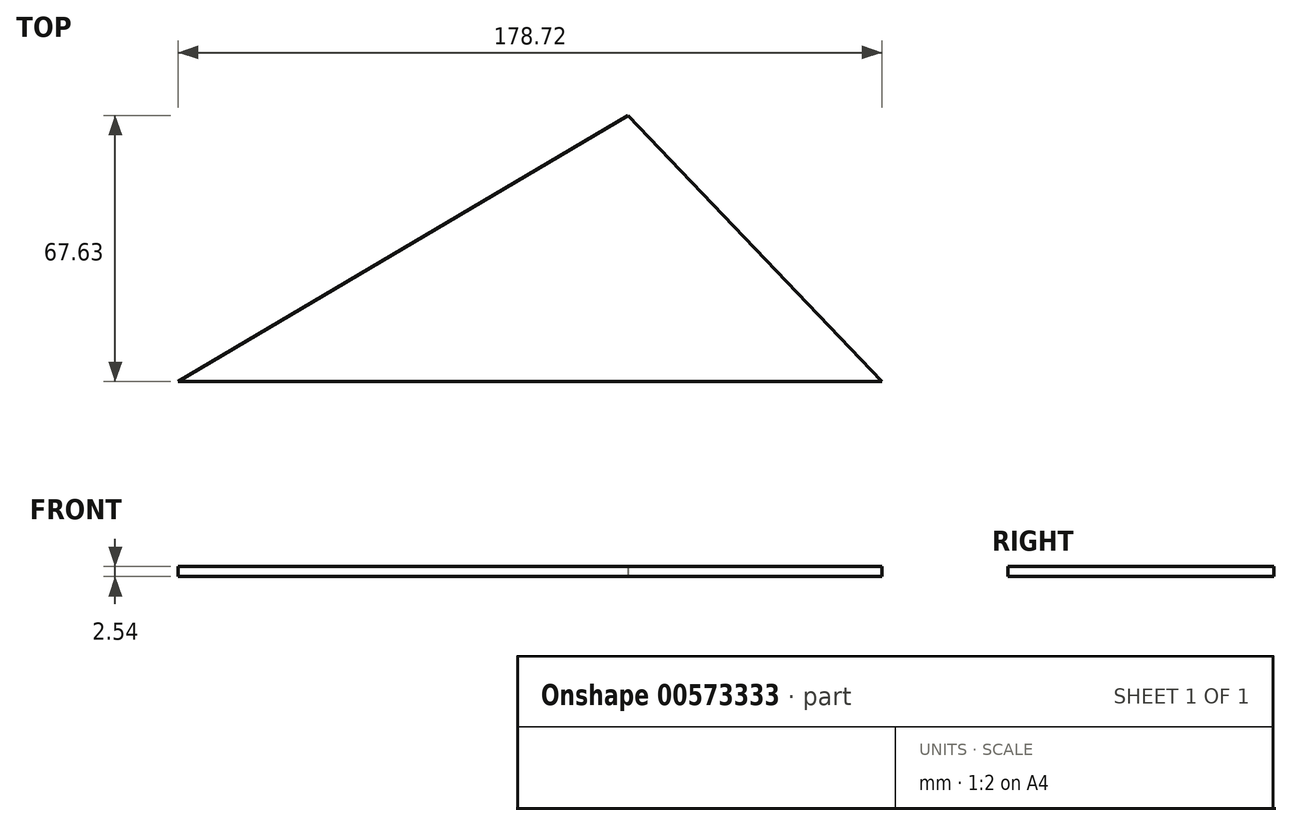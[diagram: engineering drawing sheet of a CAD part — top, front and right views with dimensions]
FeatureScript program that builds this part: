
annotation { "Feature Type Name" : "Feature", "Feature Type Description" : "" }
export const myFeature = defineFeature(function(context is Context, id is Id, definition is map)
    precondition{}
    {
        {
            var Q0;
            Q0=qCreatedBy(makeId("Top.planeOp"),FACE);
            var sketch = newSketch(context, id + "F0", { "sketchPlane" : qUnion([Q0])});
            skLineSegment(sketch, "E0", {"start": v(-94.34, 17.2) * mm, "end": v(84.38, 17.2) * mm});
            skLineSegment(sketch, "E1", {"start": v(-94.34, 17.2) * mm, "end": v(19.87, 84.84) * mm});
            skLineSegment(sketch, "E2", {"start": v(19.87, 84.84) * mm, "end": v(84.38, 17.2) * mm});
            skSolve(sketch);
        }
        {
            var Q0;
            Q0 = qSketchRegion(id + "F0", true);
            extrude(context, id + "F1", {"entities" : qUnion([Q0]), "depth" : 2.54 * mm, "offsetDistance" : 25.4 * mm});
        }
    });
